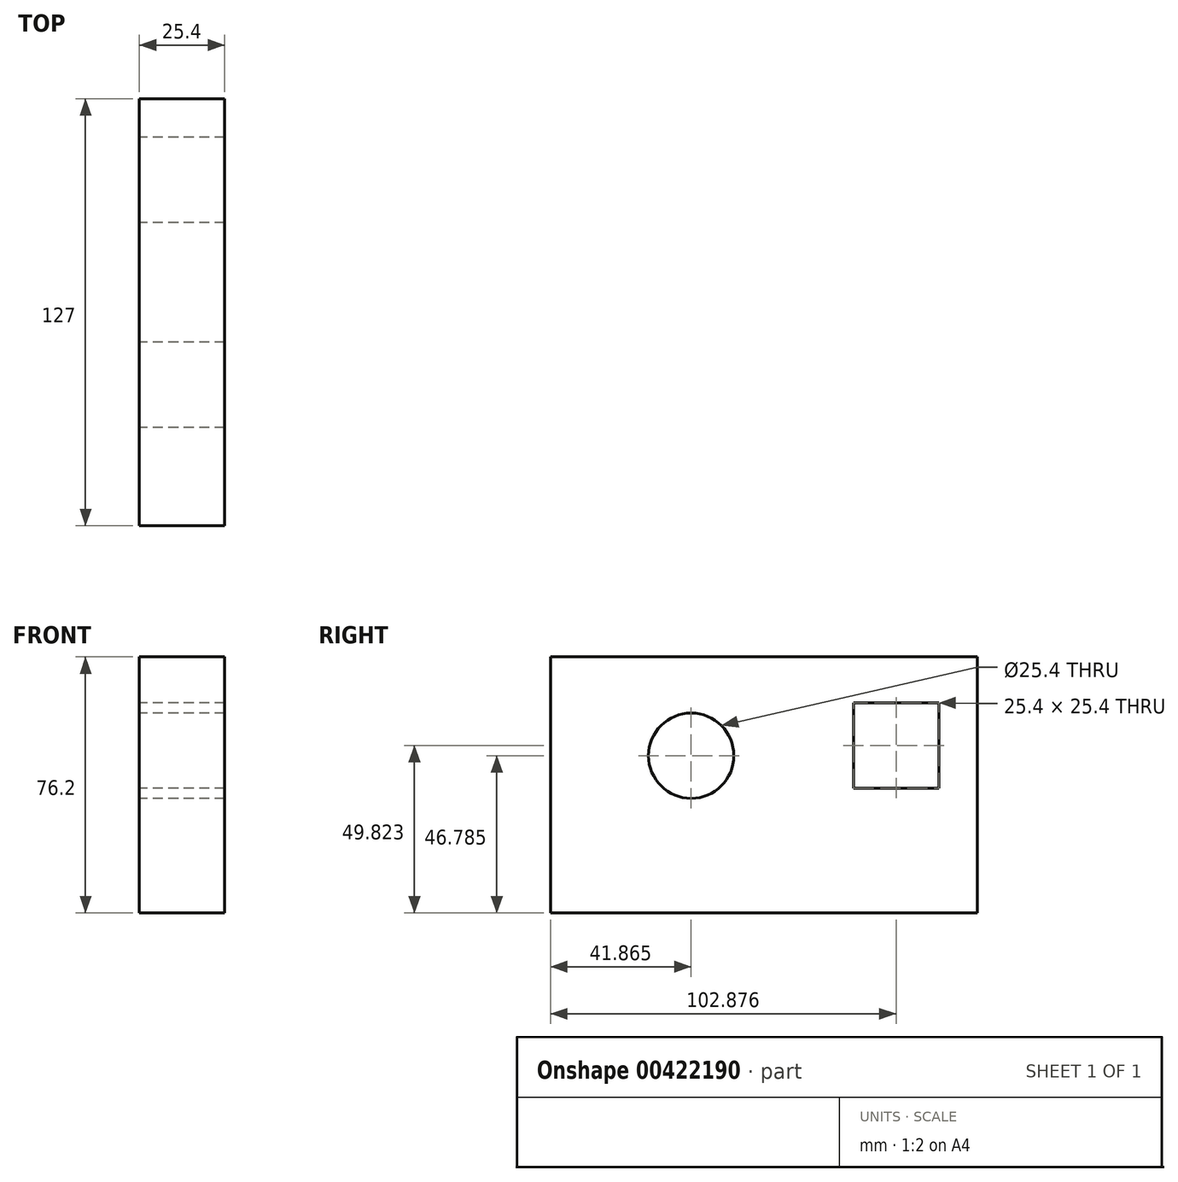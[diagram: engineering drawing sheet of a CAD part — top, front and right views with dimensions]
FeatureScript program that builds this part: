
annotation { "Feature Type Name" : "Feature", "Feature Type Description" : "" }
export const myFeature = defineFeature(function(context is Context, id is Id, definition is map)
    precondition{}
    {
        {
            var Q0;
            Q0=qCreatedBy(makeId("Right.planeOp"),FACE);
            var sketch = newSketch(context, id + "F0", { "sketchPlane" : qUnion([Q0])});
            skLineSegment(sketch, "E0", {"start": v(55.58, 0) * mm, "end": v(-71.42, 0) * mm});
            skLineSegment(sketch, "E1", {"start": v(-71.42, 0) * mm, "end": v(-71.42, 76.2) * mm});
            skLineSegment(sketch, "E2", {"start": v(-71.42, 76.2) * mm, "end": v(55.58, 76.2) * mm});
            skLineSegment(sketch, "E3", {"start": v(55.58, 76.2) * mm, "end": v(55.58, 0) * mm});
            skSolve(sketch);
        }
        {
            var Q0;
            Q0=makeQuery(id+"F0.imprint","IMPRINT",FACE,{"disambiguationData":[TD([[makeQuery(id+"F0.imprint","IMPRINT",EDGE,{"derivedFrom":sQuery(id+"F0.wireOp",EDGE,"E0")}),-1.0]])]});
            extrude(context, id + "F1", {"entities" : qUnion([Q0]), "depth" : 25.4 * mm});
        }
        {
            var Q0;
            Q0=makeQuery(id+"F1.opExtrude","CAP_FACE",FACE,{"disambiguationData":[OSD([sQuery(id+"F0.wireOp",EDGE,"E0"),sQuery(id+"F0.wireOp",EDGE,"E1"),sQuery(id+"F0.wireOp",EDGE,"E2"),sQuery(id+"F0.wireOp",EDGE,"E3")])],"isStart":true});
            var sketch = newSketch(context, id + "F2", { "sketchPlane" : qUnion([Q0])});
            skLineSegment(sketch, "E4.bottom", {"start": v(-44.16, 62.52) * mm, "end": v(-18.76, 62.52) * mm});
            skLineSegment(sketch, "E4.top", {"start": v(-44.16, 37.12) * mm, "end": v(-18.76, 37.12) * mm});
            skLineSegment(sketch, "E4.left", {"start": v(-44.16, 62.52) * mm, "end": v(-44.16, 37.12) * mm});
            skLineSegment(sketch, "E4.right", {"start": v(-18.76, 62.52) * mm, "end": v(-18.76, 37.12) * mm});
            skCircle(sketch, "E5", {"center": v(29.55, 46.79) * mm, "radius": 12.7 * mm});
            skSolve(sketch);
        }
        {
            var Q0;
            Q0 = qSketchRegion(id + "F2", true);
            extrude(context, id + "F3", {"entities" : qUnion([Q0]), "operationType" : NewBodyOperationType.REMOVE, "oppositeDirection" : true, "depth" : 2540 * mm});
        }
    });
